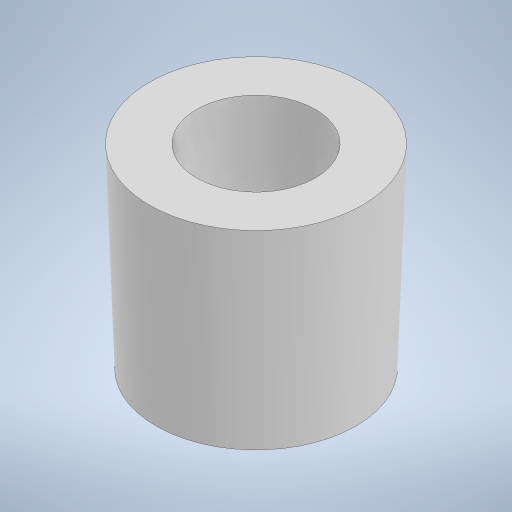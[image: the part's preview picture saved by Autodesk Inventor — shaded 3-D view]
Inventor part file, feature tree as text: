
AUTODESK INVENTOR PART (.ipt)
format: ipt  version: 2023.1 (Build 271208000, 208)  size: 210,944 bytes
history: native  units: mm
features: sketch x2, revolve x1, hole x1
ambient origin geometry x8: Origin, YZ Plane, XZ Plane, XY Plane, X Axis, Y Axis, Z Axis, Center Point
bodies: Solid1 (feature_tree)
feature tree (4):
  revolve  "Revolution1"  [1 undecoded]
  hole  "Hole1"  [1 undecoded]
  sketch  "Sketch1"  dims[d0=9.85mm d1=9.25mm]
  sketch  "Sketch2"  dims[d2=18.0mm d3=90.0deg d4=9.28mm d5=11.0mm d6=6.0mm d7=4.0mm d8=2.0mm d9=90.0deg d10=12.5mm d11=20.594885mm]
note: 2 required parameter values undecoded (feature->parameter linkage not recoverable at this tier; creation-order binding heuristic only, values carry confidence <= 0.55)